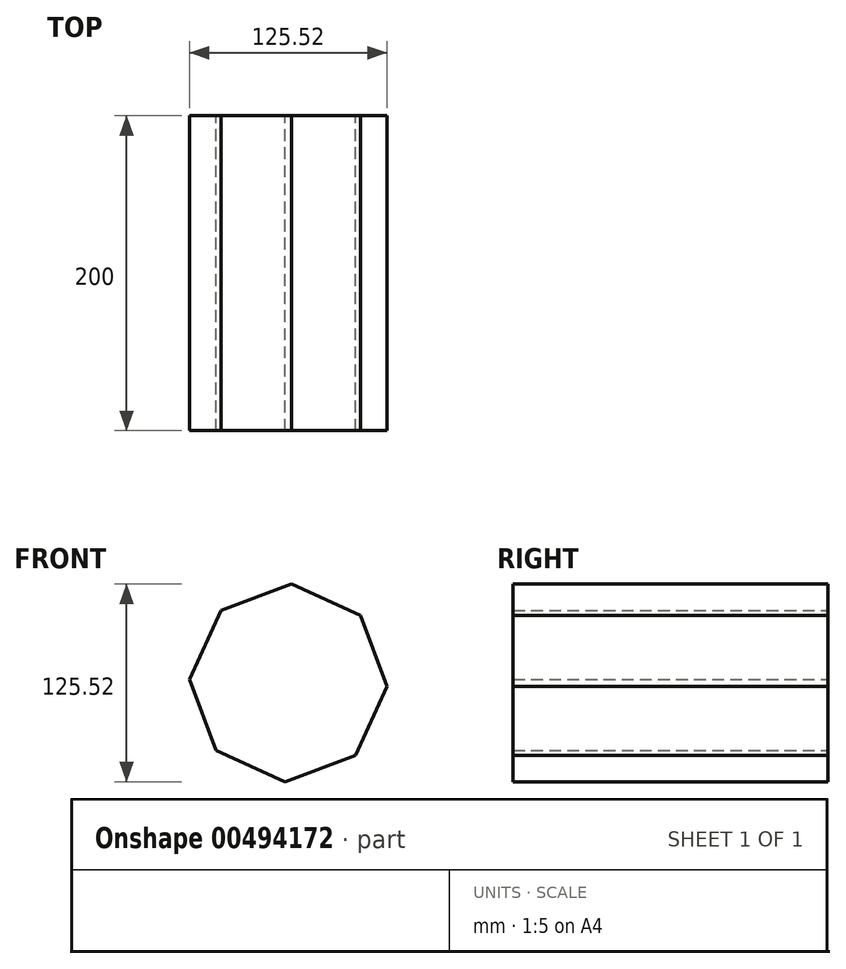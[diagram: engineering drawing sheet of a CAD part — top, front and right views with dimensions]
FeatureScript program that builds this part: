
annotation { "Feature Type Name" : "Feature", "Feature Type Description" : "" }
export const myFeature = defineFeature(function(context is Context, id is Id, definition is map)
    precondition{}
    {
        {
            var Q0;
            Q0=qCreatedBy(makeId("Front.planeOp"),FACE);
            var sketch = newSketch(context, id + "F0", { "sketchPlane" : qUnion([Q0])});
            skCircle(sketch, "E0.cCircle", {"center": v(0, 0) * mm, "radius": 62.8 * mm, "construction": true});
            skLineSegment(sketch, "E0.0", {"start": v(-42.85, 45.9) * mm, "end": v(2.16, 62.76) * mm});
            skLineSegment(sketch, "E0.1", {"start": v(2.16, 62.76) * mm, "end": v(45.9, 42.85) * mm});
            skLineSegment(sketch, "E0.2", {"start": v(45.9, 42.85) * mm, "end": v(62.76, -2.16) * mm});
            skLineSegment(sketch, "E0.3", {"start": v(62.76, -2.16) * mm, "end": v(42.85, -45.9) * mm});
            skLineSegment(sketch, "E0.4", {"start": v(42.85, -45.9) * mm, "end": v(-2.16, -62.76) * mm});
            skLineSegment(sketch, "E0.5", {"start": v(-2.16, -62.76) * mm, "end": v(-45.9, -42.85) * mm});
            skLineSegment(sketch, "E0.6", {"start": v(-45.9, -42.85) * mm, "end": v(-62.76, 2.16) * mm});
            skLineSegment(sketch, "E0.7", {"start": v(-62.76, 2.16) * mm, "end": v(-42.85, 45.9) * mm});
            skSolve(sketch);
        }
        {
            var Q0;
            Q0=makeQuery(id+"F0.imprint","IMPRINT",FACE,{"disambiguationData":[TD([[makeQuery(id+"F0.imprint","IMPRINT",EDGE,{"derivedFrom":sQuery(id+"F0.wireOp",EDGE,"E0.0")}),-1.0]])]});
            extrude(context, id + "F1", {"entities" : qUnion([Q0]), "endBound" : BoundingType.SYMMETRIC, "depth" : 200 * mm});
        }
    });
